SOLIDWORKS PART (.sldprt)
format: sldprt  version: not decoded by parser v0  size: 117,760 bytes
history: native  units: mm
features: sketch x4, cut_extrude x3, material x1, extrude x1, fillet x1 (+16 scaffold rows collapsed)
feature tree (26):
  scaffold x16  (default folders/planes/origin — collapsed)
  material  "Plain Carbon Steel"
  sketch  "Sketch1"
  extrude  "Boss-Extrude1"  Depth=6.35mm
  sketch  "Sketch2"  dims[D1=3.2mm D3=3.0mm D2=11.0mm]
  cut_extrude  "Cut-Extrude1"  [1 undecoded]
  sketch  "Sketch3"  dims[D1=6.0mm]
  cut_extrude  "Cut-Extrude2"  Depth=2.5mm
  sketch  "Sketch4"
  cut_extrude  "Cut-Extrude3"  Depth=5mm
  fillet  "Fillet1"  Radius=1mm
decode coverage: 6 of 9 modeling features carry decoded parameters
note: 1 parameter value undecoded
note: suppression state not decoded; provenance and decode notes live in map.json
